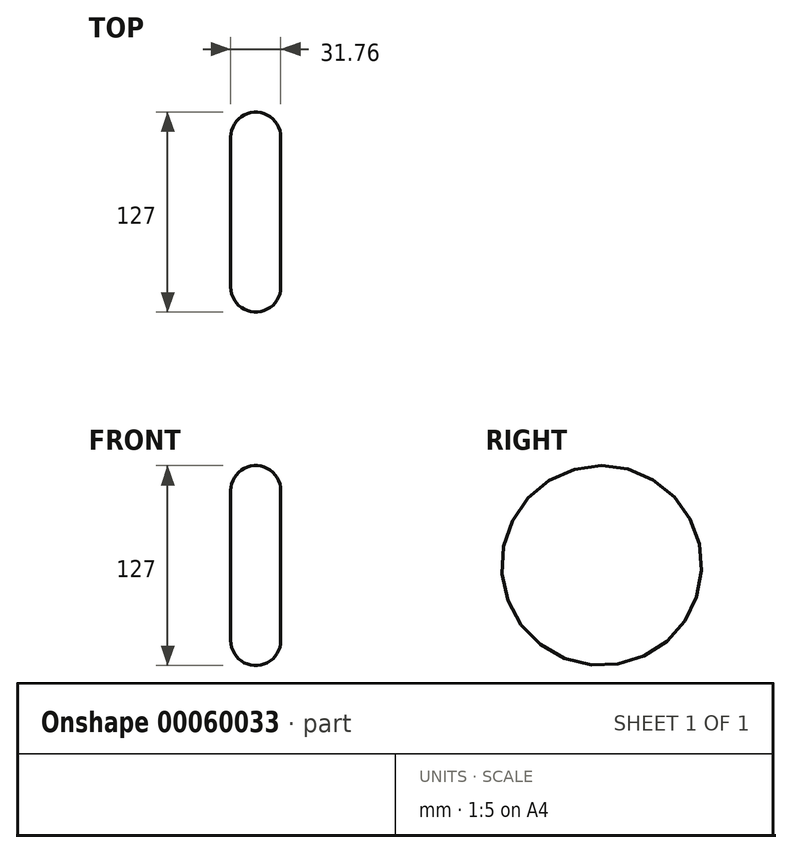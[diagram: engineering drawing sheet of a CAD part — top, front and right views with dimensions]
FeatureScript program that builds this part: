
annotation { "Feature Type Name" : "Feature", "Feature Type Description" : "" }
export const myFeature = defineFeature(function(context is Context, id is Id, definition is map)
    precondition{}
    {
        {
            var Q0;
            Q0=qCreatedBy(makeId("Front.planeOp"),FACE);
            var sketch = newSketch(context, id + "F0", { "sketchPlane" : qUnion([Q0])});
            skLineSegment(sketch, "E0.bottom", {"start": v(-15.87, 0) * mm, "end": v(15.88, 0) * mm});
            skLineSegment(sketch, "E0.top", {"start": v(-15.88, 47.62) * mm, "end": v(15.87, 47.62) * mm});
            skLineSegment(sketch, "E0.left", {"start": v(-15.87, 0) * mm, "end": v(-15.88, 47.62) * mm});
            skLineSegment(sketch, "E0.right", {"start": v(15.88, 0) * mm, "end": v(15.87, 47.62) * mm});
            skArc(sketch, "E1", {"start": v(15.87, 47.63) * mm, "mid": v(0, 63.5) * mm, "end": v(-15.88, 47.62) * mm});
            skSolve(sketch);
        }
        {
            var Q0;
            Q0=makeQuery(id+"F0.imprint","IMPRINT",FACE,{"disambiguationData":[TD([[makeQuery(id+"F0.imprint","IMPRINT",EDGE,{"derivedFrom":sQuery(id+"F0.wireOp",EDGE,"E0.top")}),1.0]])]});
            var Q1;
            Q1=makeQuery(id+"F0.imprint","IMPRINT",FACE,{"disambiguationData":[TD([[makeQuery(id+"F0.imprint","IMPRINT",EDGE,{"derivedFrom":sQuery(id+"F0.wireOp",EDGE,"E0.bottom")}),1.0]])]});
            var Q2;
            Q2=sQuery(id+"F0.wireOp",EDGE,"E0.bottom");
            revolve(context, id + "F1", {"entities" : qUnion([Q0, Q1]), "axis" : qUnion([Q2]), "revolveType" : RevolveType.FULL});
        }
    });
